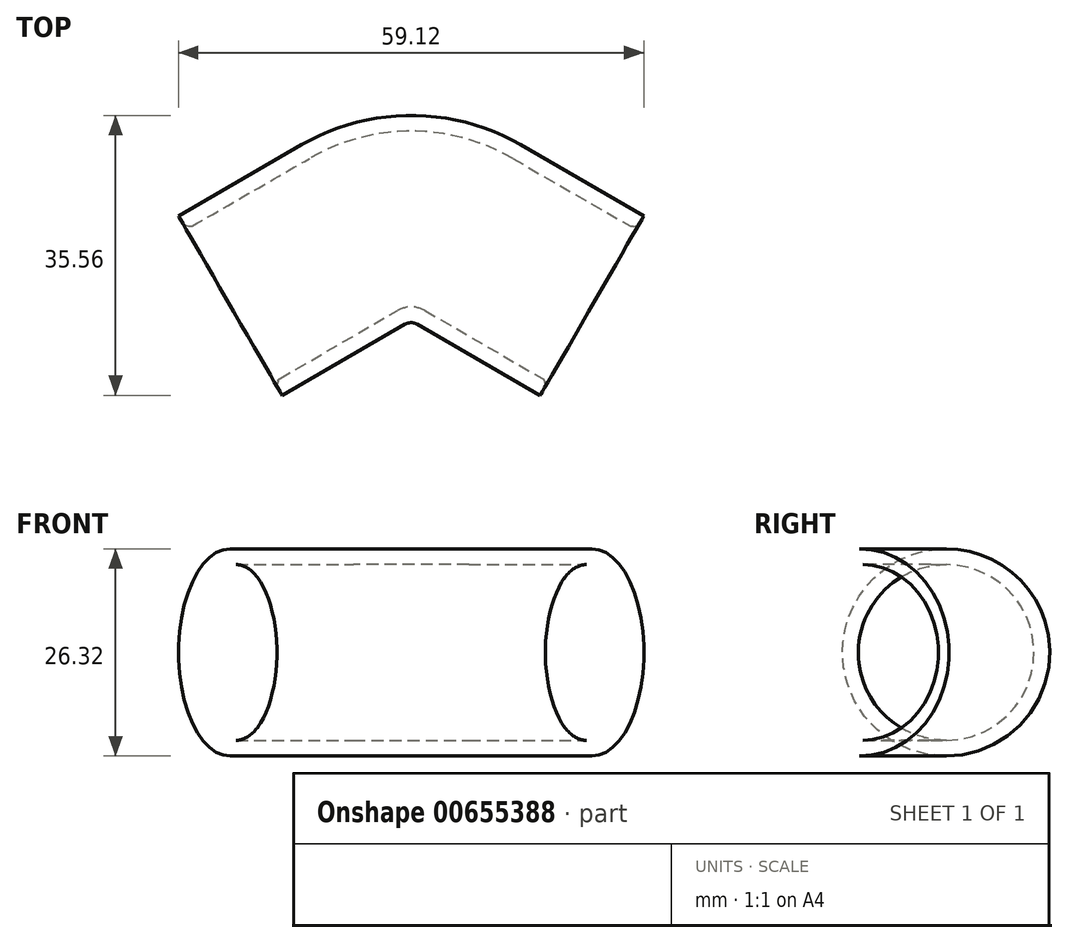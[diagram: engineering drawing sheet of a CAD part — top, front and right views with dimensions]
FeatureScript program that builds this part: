
annotation { "Feature Type Name" : "Feature", "Feature Type Description" : "" }
export const myFeature = defineFeature(function(context is Context, id is Id, definition is map)
    precondition{}
    {
        {
            var Q0;
            Q0=qCreatedBy(makeId("Top.planeOp"),FACE);
            var sketch = newSketch(context, id + "F0", { "sketchPlane" : qUnion([Q0])});
            skLineSegment(sketch, "E0", {"start": v(0, 0) * mm, "end": v(0, -12.7) * mm, "construction": true});
            skLineSegment(sketch, "E1", {"start": v(-22, -12.7) * mm, "end": v(0, -12.7) * mm, "construction": true});
            skLineSegment(sketch, "E2", {"start": v(-22, -12.7) * mm, "end": v(-6.35, -3.67) * mm});
            skLineSegment(sketch, "E3.MirrorCS", {"start": v(22, -12.7) * mm, "end": v(6.35, -3.67) * mm});
            skLineSegment(sketch, "E4.MirrorCS", {"start": v(22, -12.7) * mm, "end": v(0, -12.7) * mm, "construction": true});
            skPoint(sketch, "E5.visualSharp", {"position": v(0, 0) * mm});
            skArc(sketch, "E5.filletArc", {"start": v(6.35, -3.67) * mm, "mid": v(0, -1.96) * mm, "end": v(-6.35, -3.67) * mm});
            skSolve(sketch);
        }
        {
            var Q0;
            Q0=qCreatedBy(makeId("Right.planeOp"),FACE);
            var sketch = newSketch(context, id + "F1", { "sketchPlane" : qUnion([Q0])});
            skCircle(sketch, "E6", {"center": v(0, 0) * mm, "radius": 11.16 * mm});
            skCircle(sketch, "E7.0", {"center": v(0, 0) * mm, "radius": 13.16 * mm});
            skSolve(sketch);
        }
        {
            var Q0;
            Q0 = qSketchRegion(id + "F1", true);
            var Q1;
            Q1 = qConstructionFilter(qBodyType(qCreatedBy(id + "F0" ,EDGE), BodyType.WIRE), ConstructionObject.NO);
            sweep(context, id + "F2", {"profiles" : qUnion([Q0]), "path" : qUnion([Q1])});
        }
        {
            var Q0;
            Q0=makeQuery(id+"F2.opSweep","CAP_EDGE",EDGE,{"disambiguationData":[OSD([sQuery(id+"F0.wireOp",VERTEX,"E3.MirrorCS.start"),sQuery(id+"F1.wireOp",EDGE,"E6")])],"isStart":false});
            var Q1;
            Q1=makeQuery(id+"F2.opSweep","CAP_EDGE",EDGE,{"disambiguationData":[OSD([sQuery(id+"F0.wireOp",VERTEX,"E2.start"),sQuery(id+"F1.wireOp",EDGE,"E6")])],"isStart":true});
            chamfer(context, id + "F3", {"entities" : qUnion([Q0, Q1]), "width" : 0.64 * mm, "tangentPropagation" : true});
        }
        {
            var Q0;
            {var subQ0=sQuery(id+"F1.wireOp",EDGE,"E6");Q0=makeQuery(id+"F3.opChamfer","BLEND_EDGE",EDGE,{"blendedFrom":[makeQuery(id+"F2.opSweep","CAP_EDGE",EDGE,{"disambiguationData":[OSD([sQuery(id+"F0.wireOp",VERTEX,"E2.start"),subQ0])],"isStart":true}),makeQuery(id+"F2.opSweep","SWEPT_FACE",FACE,{"disambiguationData":[OSD([sQuery(id+"F0.wireOp",EDGE,"E2"),subQ0])]})],"blendedInto":[makeQuery(id+"F2.opSweep","SWEPT_FACE",FACE,{"disambiguationData":[OSD([sQuery(id+"F0.wireOp",EDGE,"E2"),subQ0])]})]});}
            var Q1;
            {var subQ0=sQuery(id+"F1.wireOp",EDGE,"E6");var subQ1=sQuery(id+"F0.wireOp",VERTEX,"E2.start");Q1=makeQuery(id+"F3.opChamfer","BLEND_EDGE",EDGE,{"blendedFrom":[makeQuery(id+"F2.opSweep","CAP_EDGE",EDGE,{"disambiguationData":[OSD([subQ1,subQ0])],"isStart":true}),makeQuery(id+"F2.opSweep","CAP_FACE",FACE,{"disambiguationData":[OSD([subQ1,subQ0,sQuery(id+"F1.wireOp",EDGE,"E7.0")])],"isStart":true})],"blendedInto":[makeQuery(id+"F2.opSweep","CAP_FACE",FACE,{"disambiguationData":[OSD([subQ1,subQ0,sQuery(id+"F1.wireOp",EDGE,"E7.0")])],"isStart":true})]});}
            var Q2;
            {var subQ0=sQuery(id+"F1.wireOp",EDGE,"E6");var subQ1=sQuery(id+"F0.wireOp",VERTEX,"E3.MirrorCS.start");Q2=makeQuery(id+"F3.opChamfer","BLEND_EDGE",EDGE,{"blendedFrom":[makeQuery(id+"F2.opSweep","CAP_EDGE",EDGE,{"disambiguationData":[OSD([subQ1,subQ0])],"isStart":false}),makeQuery(id+"F2.opSweep","CAP_FACE",FACE,{"disambiguationData":[OSD([subQ1,subQ0,sQuery(id+"F1.wireOp",EDGE,"E7.0")])],"isStart":false})],"blendedInto":[makeQuery(id+"F2.opSweep","CAP_FACE",FACE,{"disambiguationData":[OSD([subQ1,subQ0,sQuery(id+"F1.wireOp",EDGE,"E7.0")])],"isStart":false})]});}
            var Q3;
            {var subQ0=sQuery(id+"F1.wireOp",EDGE,"E6");Q3=makeQuery(id+"F3.opChamfer","BLEND_EDGE",EDGE,{"blendedFrom":[makeQuery(id+"F2.opSweep","CAP_EDGE",EDGE,{"disambiguationData":[OSD([sQuery(id+"F0.wireOp",VERTEX,"E3.MirrorCS.start"),subQ0])],"isStart":false}),makeQuery(id+"F2.opSweep","SWEPT_FACE",FACE,{"disambiguationData":[OSD([sQuery(id+"F0.wireOp",EDGE,"E3.MirrorCS"),subQ0])]})],"blendedInto":[makeQuery(id+"F2.opSweep","SWEPT_FACE",FACE,{"disambiguationData":[OSD([sQuery(id+"F0.wireOp",EDGE,"E3.MirrorCS"),subQ0])]})]});}
            fillet(context, id + "F4", {"entities" : qUnion([Q0, Q1, Q2, Q3]), "radius" : 0.5 * mm, "tangentPropagation" : true, "allowEdgeOverflow" : false});
        }
    });
